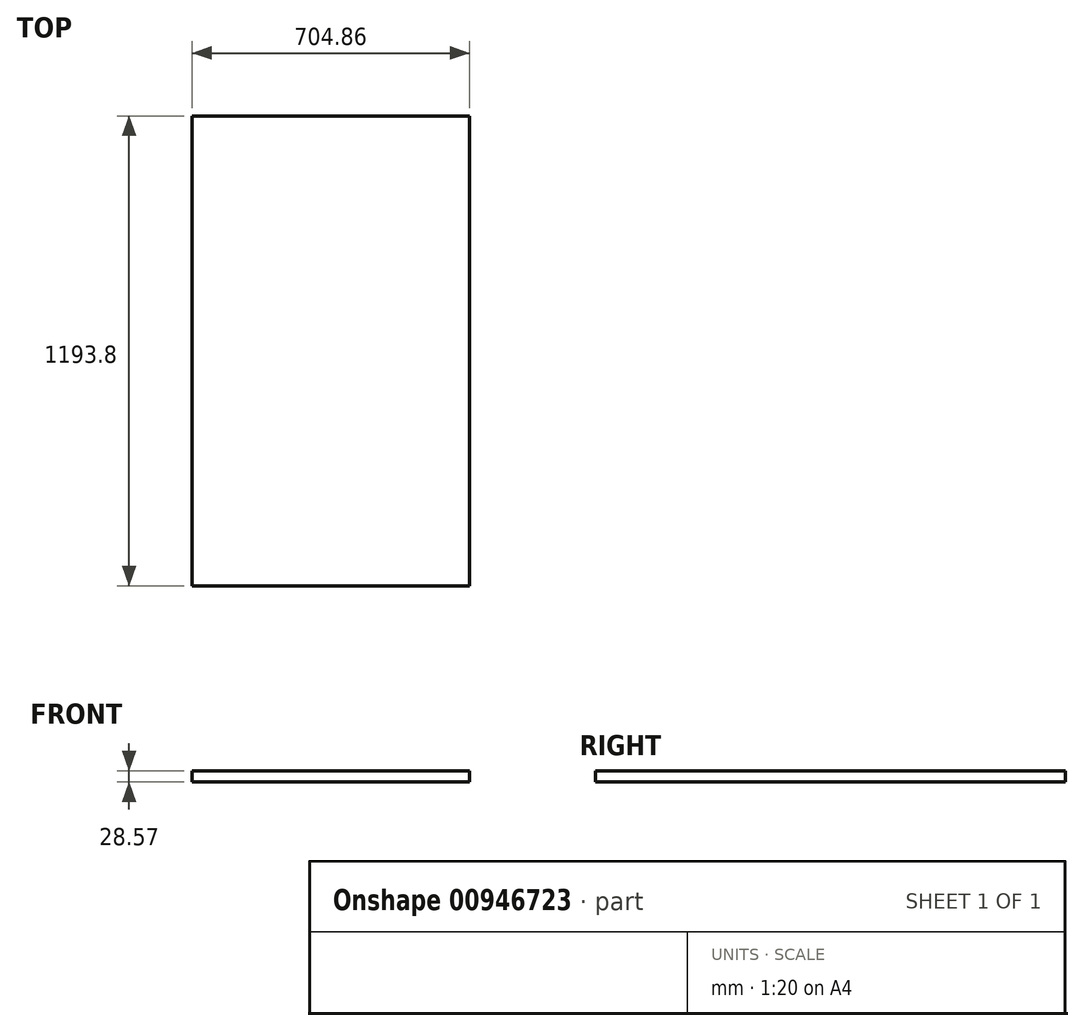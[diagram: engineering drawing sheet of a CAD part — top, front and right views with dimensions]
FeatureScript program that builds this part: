
annotation { "Feature Type Name" : "Feature", "Feature Type Description" : "" }
export const myFeature = defineFeature(function(context is Context, id is Id, definition is map)
    precondition{}
    {
        {
            var Q0;
            Q0=qCreatedBy(makeId("Top.planeOp"),FACE);
            var sketch = newSketch(context, id + "F0", { "sketchPlane" : qUnion([Q0])});
            skLineSegment(sketch, "E0.bottom", {"start": v(352.43, 596.9) * mm, "end": v(-352.43, 596.9) * mm});
            skLineSegment(sketch, "E0.top", {"start": v(352.43, -596.9) * mm, "end": v(-352.43, -596.9) * mm});
            skLineSegment(sketch, "E0.left", {"start": v(352.43, 596.9) * mm, "end": v(352.43, -596.9) * mm});
            skLineSegment(sketch, "E0.right", {"start": v(-352.43, 596.9) * mm, "end": v(-352.43, -596.9) * mm});
            skPoint(sketch, "E0.middle", {"position": v(0, 0) * mm});
            skSolve(sketch);
        }
        {
            var Q0;
            Q0=makeQuery(id+"F0.imprint","IMPRINT",FACE,{"disambiguationData":[TD([[makeQuery(id+"F0.imprint","IMPRINT",EDGE,{"derivedFrom":sQuery(id+"F0.wireOp",EDGE,"E0.bottom")}),1.0]])]});
            extrude(context, id + "F1", {"entities" : qUnion([Q0]), "depth" : 28.57 * mm, "offsetDistance" : 25.4 * mm});
        }
    });
